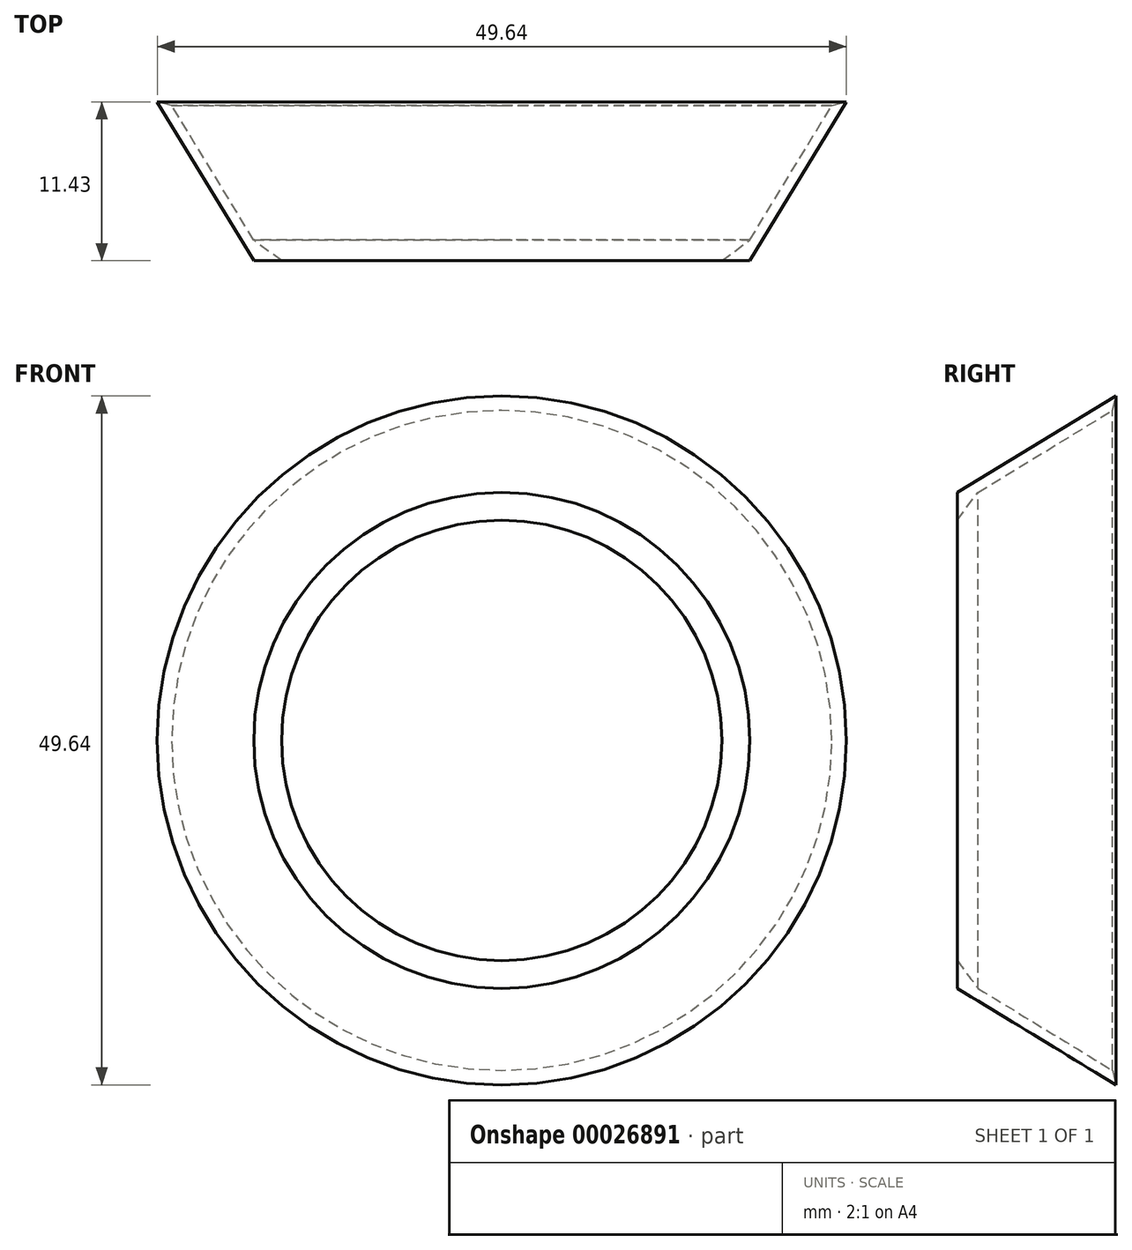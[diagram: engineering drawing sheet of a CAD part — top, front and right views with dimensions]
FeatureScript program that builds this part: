
annotation { "Feature Type Name" : "Feature", "Feature Type Description" : "" }
export const myFeature = defineFeature(function(context is Context, id is Id, definition is map)
    precondition{}
    {
        {
            var Q0;
            Q0=qCreatedBy(makeId("Top.planeOp"),FACE);
            var sketch = newSketch(context, id + "F0", { "sketchPlane" : qUnion([Q0])});
            skLineSegment(sketch, "E0", {"start": v(0, 2.13) * mm, "end": v(0, 12.32) * mm});
            skSolve(sketch);
        }
        {
            var Q0;
            Q0=qCreatedBy(makeId("Top.planeOp"),FACE);
            var sketch = newSketch(context, id + "F1", { "sketchPlane" : qUnion([Q0])});
            skLineSegment(sketch, "E1", {"start": v(24.82, 23.9) * mm, "end": v(17.87, 12.46) * mm});
            skLineSegment(sketch, "E2", {"start": v(17.87, 12.46) * mm, "end": v(16.97, 12.46) * mm});
            skLineSegment(sketch, "E3", {"start": v(16.97, 12.46) * mm, "end": v(23.78, 23.65) * mm});
            skLineSegment(sketch, "E4", {"start": v(23.78, 23.65) * mm, "end": v(24.82, 23.9) * mm});
            skLineSegment(sketch, "E5", {"start": v(16.97, 12.46) * mm, "end": v(15.87, 12.46) * mm});
            skLineSegment(sketch, "E6", {"start": v(15.87, 12.46) * mm, "end": v(17.88, 13.95) * mm});
            skSolve(sketch);
        }
        {
            var Q0;
            Q0 = qSketchRegion(id + "F1", true);
            var Q1;
            Q1=sQuery(id+"F0.wireOp",EDGE,"E0");
            revolve(context, id + "F2", {"entities" : qUnion([Q0]), "axis" : qUnion([Q1]), "revolveType" : RevolveType.FULL});
        }
    });
